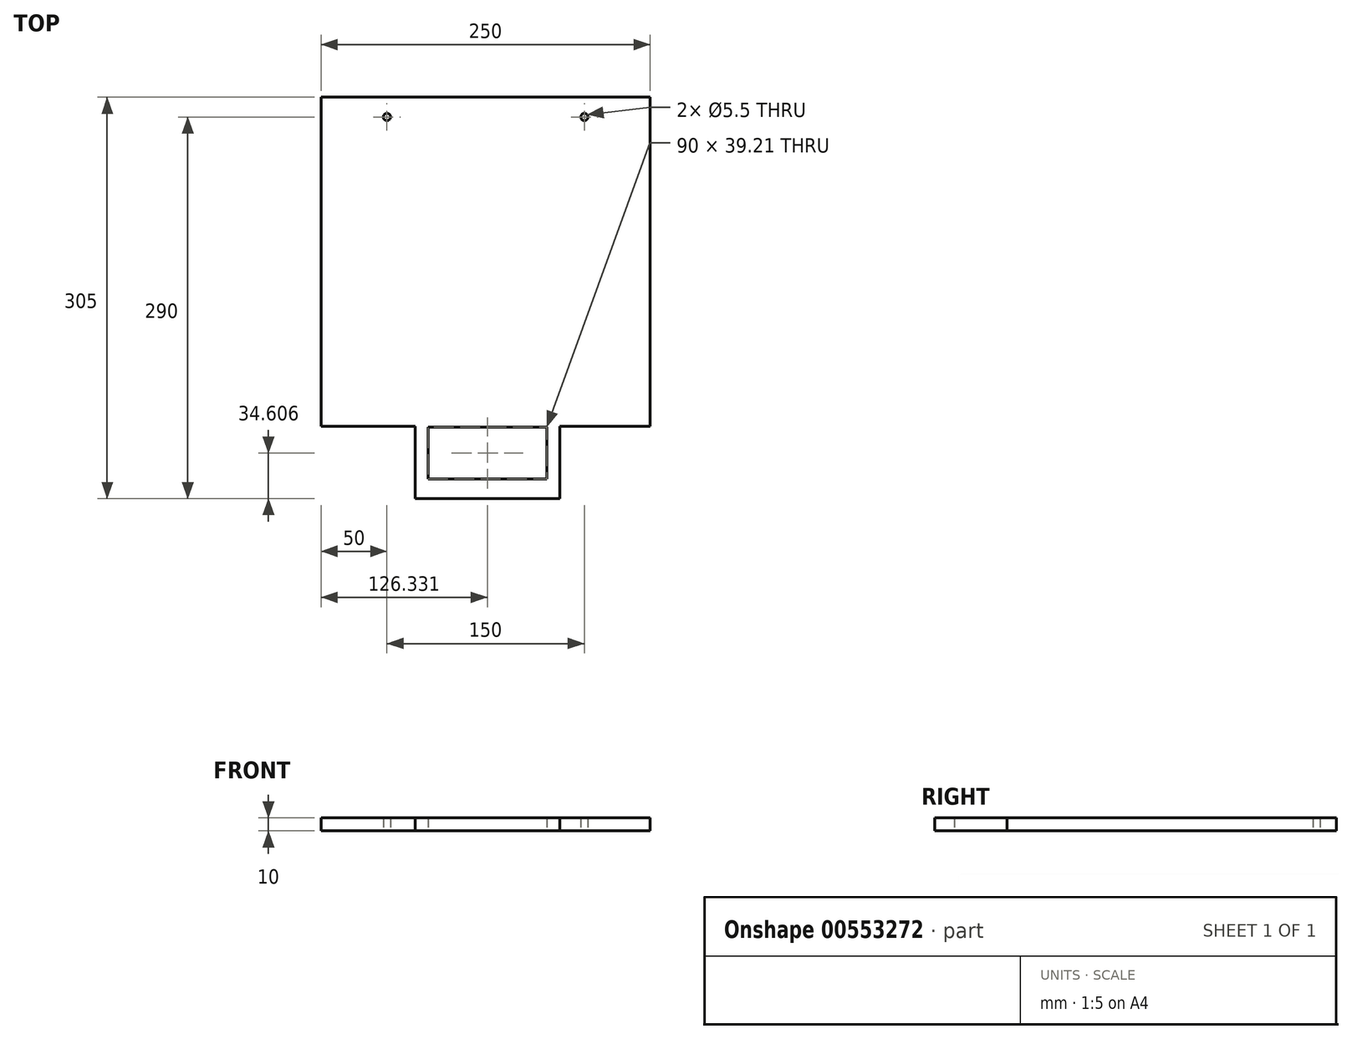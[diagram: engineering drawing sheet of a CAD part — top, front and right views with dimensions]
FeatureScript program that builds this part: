
annotation { "Feature Type Name" : "Feature", "Feature Type Description" : "" }
export const myFeature = defineFeature(function(context is Context, id is Id, definition is map)
    precondition{}
    {
        {
            var Q0;
            Q0=qCreatedBy(makeId("Top.planeOp"),FACE);
            var sketch = newSketch(context, id + "F0", { "sketchPlane" : qUnion([Q0])});
            skLineSegment(sketch, "E0.bottom", {"start": v(125, 125) * mm, "end": v(-125, 125) * mm});
            skLineSegment(sketch, "E0.top", {"start": v(125, -125) * mm, "end": v(-125, -125) * mm});
            skLineSegment(sketch, "E0.left", {"start": v(125, 125) * mm, "end": v(125, -125) * mm});
            skLineSegment(sketch, "E0.right", {"start": v(-125, 125) * mm, "end": v(-125, -125) * mm});
            skPoint(sketch, "E0.middle", {"position": v(0, 0) * mm});
            skPoint(sketch, "E1", {"position": v(-12.18, -125.79) * mm});
            skLineSegment(sketch, "E2.bottom", {"start": v(-43.67, -125.79) * mm, "end": v(-43.67, -165) * mm});
            skLineSegment(sketch, "E2.top", {"start": v(46.33, -125.79) * mm, "end": v(46.33, -165) * mm});
            skLineSegment(sketch, "E2.left", {"start": v(-43.67, -125.79) * mm, "end": v(46.33, -125.79) * mm});
            skLineSegment(sketch, "E2.right", {"start": v(-43.67, -165) * mm, "end": v(46.33, -165) * mm});
            skLineSegment(sketch, "E3.bottom", {"start": v(-53.67, -125) * mm, "end": v(-53.67, -180) * mm});
            skLineSegment(sketch, "E3.top", {"start": v(56.33, -125) * mm, "end": v(56.33, -180) * mm});
            skLineSegment(sketch, "E3.left", {"start": v(-53.67, -125) * mm, "end": v(56.33, -125) * mm});
            skLineSegment(sketch, "E3.right", {"start": v(-53.67, -180) * mm, "end": v(56.33, -180) * mm});
            skPoint(sketch, "E4", {"position": v(-75, 110) * mm});
            skPoint(sketch, "E5", {"position": v(75, 110) * mm});
            skSolve(sketch);
        }
        {
            var Q0;
            Q0 = qSketchRegion(id + "F0", true);
            extrude(context, id + "F1", {"entities" : qUnion([Q0]), "depth" : 10 * mm, "offsetDistance" : 25 * mm});
        }
        {
            var Q0;
            Q0=sQuery(id+"F0.wireOp",VERTEX,"E4");
            var Q1;
            Q1=sQuery(id+"F0.wireOp",VERTEX,"E5");
            var Q2;
            Q2=makeQuery(id+"F1.opExtrude","SWEPT_BODY",BODY,{"disambiguationData":[OSD([sQuery(id+"F0.wireOp",EDGE,"E0.bottom"),sQuery(id+"F0.wireOp",EDGE,"E0.top"),sQuery(id+"F0.wireOp",EDGE,"E0.left"),sQuery(id+"F0.wireOp",EDGE,"E0.right"),sQuery(id+"F0.wireOp",EDGE,"E2.bottom"),sQuery(id+"F0.wireOp",EDGE,"E2.top"),sQuery(id+"F0.wireOp",EDGE,"E2.left"),sQuery(id+"F0.wireOp",EDGE,"E2.right"),sQuery(id+"F0.wireOp",EDGE,"E3.bottom"),sQuery(id+"F0.wireOp",EDGE,"E3.top"),sQuery(id+"F0.wireOp",EDGE,"E3.right")])]});
            hole(context, id + "F2", {"style" : HoleStyle.SIMPLE, "endStyle" : HoleEndStyle.THROUGH, "oppositeDirection" : true, "holeDiameter" : 5.5 * mm, "isTappedThrough" : true, "tappedDepth" : 12 * mm, "tapClearance" : 3, "locations" : qUnion([Q0, Q1]), "scope" : qUnion([Q2])});
        }
    });
